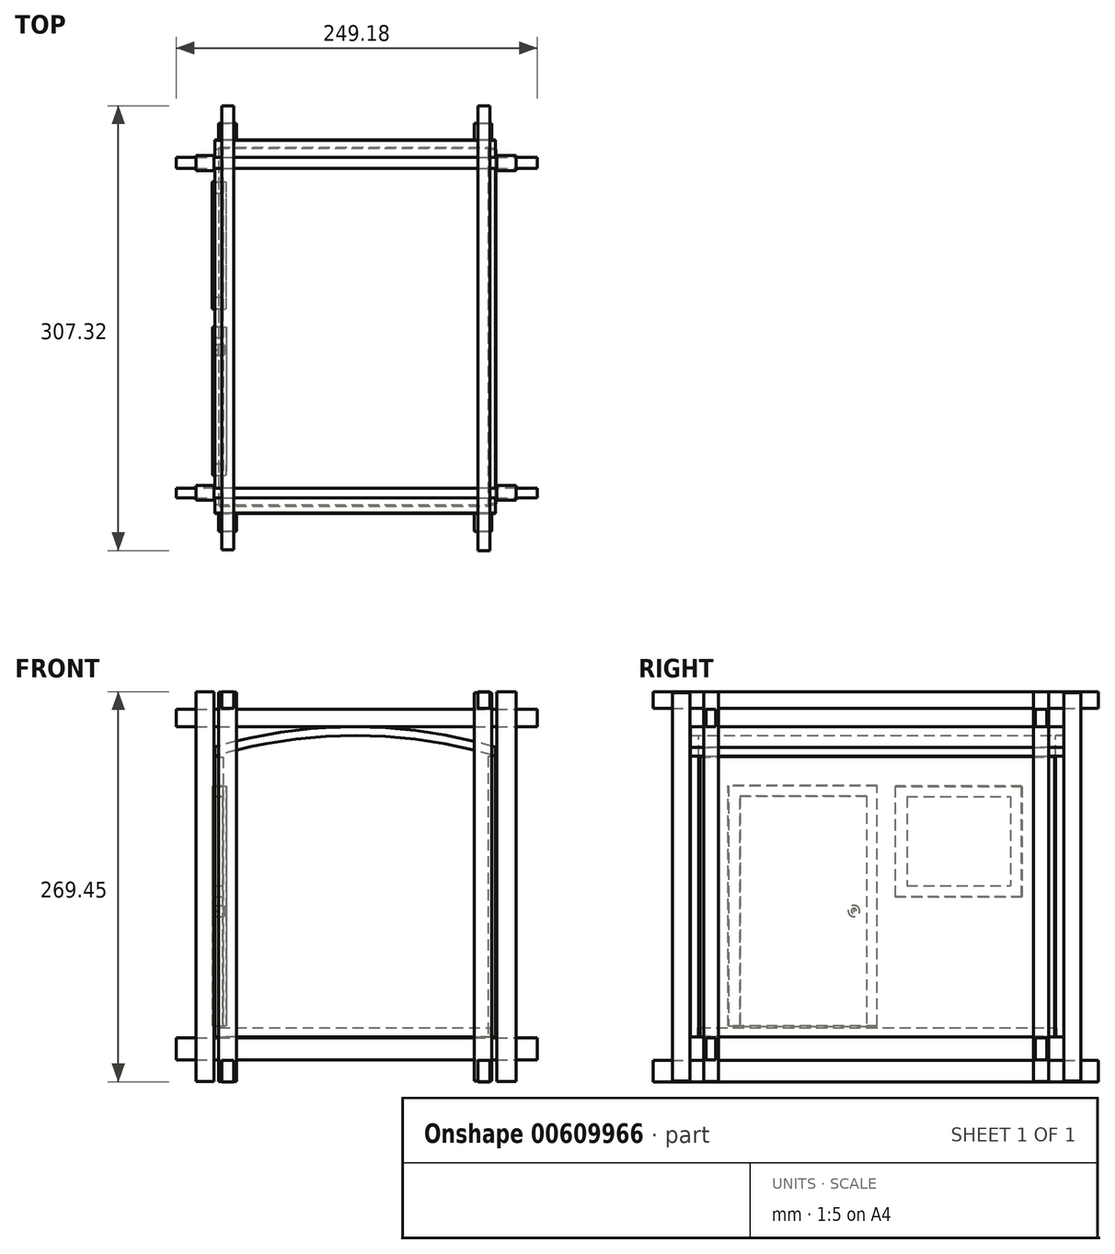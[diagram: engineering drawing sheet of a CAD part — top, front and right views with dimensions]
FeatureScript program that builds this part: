
annotation { "Feature Type Name" : "Feature", "Feature Type Description" : "" }
export const myFeature = defineFeature(function(context is Context, id is Id, definition is map)
    precondition{}
    {
        {
            var Q0;
            Q0=qCreatedBy(makeId("Front.planeOp"),FACE);
            var sketch = newSketch(context, id + "F0", { "sketchPlane" : qUnion([Q0])});
            skLineSegment(sketch, "E0", {"start": v(97.04, 97.04) * mm, "end": v(97.04, -96.89) * mm});
            skLineSegment(sketch, "E1", {"start": v(97.04, -96.89) * mm, "end": v(-96.89, -96.89) * mm});
            skLineSegment(sketch, "E2", {"start": v(-96.89, 97.04) * mm, "end": v(-96.89, -96.89) * mm});
            skArc(sketch, "E3", {"start": v(97.04, 97.04) * mm, "mid": v(0.08, 111.29) * mm, "end": v(-96.89, 97.04) * mm});
            skLineSegment(sketch, "E4", {"start": v(-96.89, 103.37) * mm, "end": v(-96.89, 97.04) * mm});
            skPoint(sketch, "E5.startSnap0", {"position": v(0.08, 111.29) * mm});
            skArc(sketch, "E6", {"start": v(97.04, 103.19) * mm, "mid": v(0.09, 117.3) * mm, "end": v(-96.89, 103.37) * mm});
            skLineSegment(sketch, "E7", {"start": v(97.04, 103.19) * mm, "end": v(97.04, 97.04) * mm});
            skSolve(sketch);
        }
        {
            var Q0;
            Q0=qCreatedBy(makeId("Right.planeOp"),FACE);
            var sketch = newSketch(context, id + "F1", { "sketchPlane" : qUnion([Q0])});
            skLineSegment(sketch, "E8.bottom", {"start": v(-124, 96.59) * mm, "end": v(124, 96.59) * mm});
            skLineSegment(sketch, "E8.top", {"start": v(-124, -96.59) * mm, "end": v(124, -96.59) * mm});
            skLineSegment(sketch, "E8.left", {"start": v(-124, 96.59) * mm, "end": v(-124, -96.59) * mm});
            skLineSegment(sketch, "E8.right", {"start": v(124, 96.59) * mm, "end": v(124, -96.59) * mm});
            skPoint(sketch, "E8.middle", {"position": v(0, 0) * mm});
            skLineSegment(sketch, "E9.bottom", {"start": v(100.14, 0) * mm, "end": v(11.51, 0) * mm});
            skLineSegment(sketch, "E9.top", {"start": v(100.14, 76.42) * mm, "end": v(11.51, 76.42) * mm});
            skLineSegment(sketch, "E9.left", {"start": v(100.14, 0) * mm, "end": v(100.14, 76.42) * mm});
            skLineSegment(sketch, "E9.right", {"start": v(11.51, 0) * mm, "end": v(11.51, 76.42) * mm});
            skLineSegment(sketch, "E10.bottom", {"start": v(17.87, 69.87) * mm, "end": v(93.79, 69.87) * mm});
            skLineSegment(sketch, "E10.top", {"start": v(17.87, 6.55) * mm, "end": v(93.79, 6.55) * mm});
            skLineSegment(sketch, "E10.left", {"start": v(17.87, 69.87) * mm, "end": v(17.87, 6.55) * mm});
            skLineSegment(sketch, "E10.right", {"start": v(93.79, 69.87) * mm, "end": v(93.79, 6.55) * mm});
            skPoint(sketch, "E10.middle", {"position": v(55.83, 38.21) * mm});
            skSolve(sketch);
        }
        {
            var Q0;
            Q0=makeQuery(id+"F0.imprint","IMPRINT",FACE,{"disambiguationData":[TD([[makeQuery(id+"F0.imprint","IMPRINT",EDGE,{"derivedFrom":sQuery(id+"F0.wireOp",EDGE,"E0")}),-1.0]])]});
            var sketch = newSketch(context, id + "F2", { "sketchPlane" : qUnion([Q0])});
            skSolve(sketch);
        }
        {
            var Q0;
            Q0=makeQuery(id+"F0.imprint","IMPRINT",FACE,{"disambiguationData":[TD([[makeQuery(id+"F0.imprint","IMPRINT",EDGE,{"derivedFrom":sQuery(id+"F0.wireOp",EDGE,"E0")}),-1.0]])]});
            extrude(context, id + "F3", {"entities" : qUnion([Q0]), "oppositeDirection" : true, "depth" : 128.86 * mm, "offsetDistance" : 25.4 * mm, "hasSecondDirection" : true, "secondDirectionOppositeDirection" : true, "secondDirectionDepth" : 123.07 * mm});
        }
        {
            var Q0;
            Q0=qCreatedBy(makeId("Top.planeOp"),FACE);
            var sketch = newSketch(context, id + "F4", { "sketchPlane" : qUnion([Q0])});
            skLineSegment(sketch, "E11.bottom", {"start": v(-93.76, -123.94) * mm, "end": v(93.76, -123.94) * mm});
            skLineSegment(sketch, "E11.top", {"start": v(-93.76, 123.94) * mm, "end": v(93.76, 123.94) * mm});
            skLineSegment(sketch, "E11.left", {"start": v(-93.76, -123.94) * mm, "end": v(-93.76, 123.94) * mm});
            skLineSegment(sketch, "E11.right", {"start": v(93.76, -123.94) * mm, "end": v(93.76, 123.94) * mm});
            skPoint(sketch, "E11.middle", {"position": v(0, 0) * mm});
            skSolve(sketch);
        }
        {
            var Q0;
            Q0=makeQuery(id+"F4.imprint","IMPRINT",FACE,{"disambiguationData":[TD([[makeQuery(id+"F4.imprint","IMPRINT",EDGE,{"derivedFrom":sQuery(id+"F4.wireOp",EDGE,"E11.bottom")}),1.0]])]});
            extrude(context, id + "F5", {"entities" : qUnion([Q0]), "oppositeDirection" : true, "depth" : 97.05 * mm, "offsetDistance" : 25.4 * mm, "hasSecondDirection" : true, "secondDirectionOppositeDirection" : true, "secondDirectionDepth" : 90.61 * mm});
        }
        {
            var Q0;
            Q0=makeQuery(id+"F0.imprint","IMPRINT",FACE,{"disambiguationData":[TD([[makeQuery(id+"F0.imprint","IMPRINT",EDGE,{"derivedFrom":sQuery(id+"F0.wireOp",EDGE,"E3")}),-1.0]])]});
            extrude(context, id + "F6", {"entities" : qUnion([Q0]), "depth" : 128.9 * mm, "offsetDistance" : 25.4 * mm, "hasSecondDirection" : true, "secondDirectionOppositeDirection" : true, "secondDirectionDepth" : 128.7 * mm});
        }
        {
            var Q0;
            Q0=makeQuery(id+"F2.imprint","IMPRINT",FACE,{"disambiguationData":[TD([[makeQuery(id+"F2.imprint","IMPRINT",EDGE,{"derivedFrom":makeQuery(id+"F0.imprint","IMPRINT",EDGE,{"derivedFrom":sQuery(id+"F0.wireOp",EDGE,"E0")})}),-1.0]])]});
            extrude(context, id + "F7", {"entities" : qUnion([Q0]), "depth" : 129.08 * mm, "offsetDistance" : 25.4 * mm, "hasSecondDirection" : true, "secondDirectionOppositeDirection" : false, "secondDirectionDepth" : 123.47 * mm});
        }
        {
            var Q0;
            Q0=qCreatedBy(makeId("Right.planeOp"),FACE);
            var sketch = newSketch(context, id + "F8", { "sketchPlane" : qUnion([Q0])});
            skLineSegment(sketch, "E12.bottom", {"start": v(122.43, 96.89) * mm, "end": v(-122.43, 96.89) * mm});
            skLineSegment(sketch, "E12.top", {"start": v(122.43, -96.89) * mm, "end": v(-122.43, -96.89) * mm});
            skLineSegment(sketch, "E12.left", {"start": v(122.43, 96.89) * mm, "end": v(122.43, -96.89) * mm});
            skLineSegment(sketch, "E12.right", {"start": v(-122.43, 96.89) * mm, "end": v(-122.43, -96.89) * mm});
            skPoint(sketch, "E12.middle", {"position": v(0, 0) * mm});
            skSolve(sketch);
        }
        {
            var Q0;
            Q0=qSketchRegion(id+"F8",true);
            extrude(context, id + "F9", {"entities" : qUnion([Q0]), "depth" : 97.34 * mm, "offsetDistance" : 25.4 * mm, "hasSecondDirection" : true, "secondDirectionOppositeDirection" : false, "secondDirectionDepth" : 91.88 * mm});
        }
        {
            var Q0;
            Q0=qCreatedBy(makeId("Right.planeOp"),FACE);
            var sketch = newSketch(context, id + "F10", { "sketchPlane" : qUnion([Q0])});
            skLineSegment(sketch, "E13.bottom", {"start": v(-122.74, 96.39) * mm, "end": v(122.74, 96.39) * mm});
            skLineSegment(sketch, "E13.top", {"start": v(-122.74, -96.39) * mm, "end": v(122.74, -96.39) * mm});
            skLineSegment(sketch, "E13.left", {"start": v(-122.74, 96.39) * mm, "end": v(-122.74, -96.39) * mm});
            skLineSegment(sketch, "E13.right", {"start": v(122.74, 96.39) * mm, "end": v(122.74, -96.39) * mm});
            skPoint(sketch, "E13.middle", {"position": v(0, 0) * mm});
            skLineSegment(sketch, "E14.bottom", {"start": v(99.68, 0) * mm, "end": v(12.53, 0) * mm});
            skLineSegment(sketch, "E14.top", {"start": v(99.68, 76.43) * mm, "end": v(12.53, 76.43) * mm});
            skLineSegment(sketch, "E14.left", {"start": v(99.68, 0) * mm, "end": v(99.68, 76.43) * mm});
            skLineSegment(sketch, "E14.right", {"start": v(12.53, 0) * mm, "end": v(12.53, 76.43) * mm});
            skLineSegment(sketch, "E15.bottom", {"start": v(20.07, 69.11) * mm, "end": v(92.14, 69.11) * mm});
            skLineSegment(sketch, "E15.top", {"start": v(20.07, 7.32) * mm, "end": v(92.14, 7.32) * mm});
            skLineSegment(sketch, "E15.left", {"start": v(20.07, 69.11) * mm, "end": v(20.07, 7.32) * mm});
            skLineSegment(sketch, "E15.right", {"start": v(92.14, 69.11) * mm, "end": v(92.14, 7.32) * mm});
            skPoint(sketch, "E15.middle", {"position": v(56.1, 38.22) * mm});
            skLineSegment(sketch, "E16", {"start": v(0, 0) * mm, "end": v(0, -89.44) * mm});
            skLineSegment(sketch, "E17.bottom", {"start": v(0, -89.44) * mm, "end": v(-102.94, -89.44) * mm});
            skLineSegment(sketch, "E17.top", {"start": v(0, 76.65) * mm, "end": v(-102.94, 76.65) * mm});
            skLineSegment(sketch, "E17.left", {"start": v(0, -89.44) * mm, "end": v(0, 76.65) * mm});
            skLineSegment(sketch, "E17.right", {"start": v(-102.94, -89.44) * mm, "end": v(-102.94, 76.65) * mm});
            skSolve(sketch);
        }
        {
            var Q0;
            Q0=makeQuery(id+"F10.imprint","IMPRINT",FACE,{"disambiguationData":[TD([[makeQuery(id+"F10.imprint","IMPRINT",EDGE,{"derivedFrom":sQuery(id+"F10.wireOp",EDGE,"E13.bottom")}),-1.0]])]});
            extrude(context, id + "F11", {"entities" : qUnion([Q0]), "operationType" : NewBodyOperationType.ADD, "oppositeDirection" : true, "depth" : 96.6 * mm, "offsetDistance" : 25.4 * mm, "hasSecondDirection" : true, "secondDirectionOppositeDirection" : true, "secondDirectionDepth" : 90.9 * mm});
        }
        {
            var Q0;
            Q0=makeQuery(id+"F10.imprint","IMPRINT",FACE,{"disambiguationData":[TD([[makeQuery(id+"F10.imprint","IMPRINT",EDGE,{"derivedFrom":sQuery(id+"F10.wireOp",EDGE,"E14.bottom")}),-1.0]])]});
            var Q1;
            Q1=qSketchRegion(id+"F10",true);
            extrude(context, id + "F12", {"entities" : qUnion([Q0, Q1]), "depth" : 25.4 * mm, "offsetDistance" : 25.4 * mm});
        }
        {
            var Q0;
            Q0=makeQuery(id+"F12.opExtrude","SWEPT_BODY",BODY,{"disambiguationData":[OSD([sQuery(id+"F10.wireOp",EDGE,"E13.bottom"),sQuery(id+"F10.wireOp",EDGE,"E13.top"),sQuery(id+"F10.wireOp",EDGE,"E13.left"),sQuery(id+"F10.wireOp",EDGE,"E13.right"),sQuery(id+"F10.wireOp",EDGE,"E15.bottom"),sQuery(id+"F10.wireOp",EDGE,"E15.top"),sQuery(id+"F10.wireOp",EDGE,"E15.left"),sQuery(id+"F10.wireOp",EDGE,"E15.right"),sQuery(id+"F10.wireOp",EDGE,"E17.bottom"),sQuery(id+"F10.wireOp",EDGE,"E17.top"),sQuery(id+"F10.wireOp",EDGE,"E17.left"),sQuery(id+"F10.wireOp",EDGE,"E17.right")])]});
            deleteBodies(context, id + "F13", {"entities" : qUnion([Q0])});
        }
        {
            var Q0;
            Q0=qCreatedBy(makeId("Right.planeOp"),FACE);
            var sketch = newSketch(context, id + "F14", { "sketchPlane" : qUnion([Q0])});
            skLineSegment(sketch, "E18.bottom", {"start": v(12.24, 76.08) * mm, "end": v(100.02, 76.08) * mm});
            skLineSegment(sketch, "E18.top", {"start": v(12.24, -0.18) * mm, "end": v(100.02, -0.18) * mm});
            skLineSegment(sketch, "E18.left", {"start": v(12.24, 76.08) * mm, "end": v(12.24, -0.18) * mm});
            skLineSegment(sketch, "E18.right", {"start": v(100.02, 76.08) * mm, "end": v(100.02, -0.18) * mm});
            skLineSegment(sketch, "E19.bottom", {"start": v(20.4, 68.99) * mm, "end": v(92.04, 68.99) * mm});
            skLineSegment(sketch, "E19.top", {"start": v(20.4, 7.45) * mm, "end": v(92.04, 7.45) * mm});
            skLineSegment(sketch, "E19.left", {"start": v(20.4, 68.99) * mm, "end": v(20.4, 7.45) * mm});
            skLineSegment(sketch, "E19.right", {"start": v(92.04, 68.99) * mm, "end": v(92.04, 7.45) * mm});
            skSolve(sketch);
        }
        {
            var Q0;
            Q0=makeQuery(id+"F14.imprint","IMPRINT",FACE,{"disambiguationData":[TD([[makeQuery(id+"F14.imprint","IMPRINT",EDGE,{"derivedFrom":sQuery(id+"F14.wireOp",EDGE,"E18.bottom")}),-1.0]])]});
            extrude(context, id + "F15", {"entities" : qUnion([Q0]), "oppositeDirection" : true, "depth" : 98.51 * mm, "offsetDistance" : 25.4 * mm, "hasSecondDirection" : true, "secondDirectionOppositeDirection" : true, "secondDirectionDepth" : 88.94 * mm});
        }
        {
            var Q0;
            Q0=qCreatedBy(makeId("Right.planeOp"),FACE);
            var sketch = newSketch(context, id + "F16", { "sketchPlane" : qUnion([Q0])});
            skLineSegment(sketch, "E20.bottom", {"start": v(-94.62, 69.34) * mm, "end": v(-7.44, 69.34) * mm});
            skLineSegment(sketch, "E20.top", {"start": v(-94.62, -89.54) * mm, "end": v(-7.44, -89.54) * mm});
            skLineSegment(sketch, "E20.left", {"start": v(-94.62, 69.34) * mm, "end": v(-94.62, -89.54) * mm});
            skLineSegment(sketch, "E20.right", {"start": v(-7.44, 69.34) * mm, "end": v(-7.44, -89.54) * mm});
            skPoint(sketch, "E20.middle", {"position": v(-51.03, -10.1) * mm});
            skSolve(sketch);
        }
        {
            var Q0;
            Q0=makeQuery(id+"F16.imprint","IMPRINT",FACE,{"disambiguationData":[TD([[makeQuery(id+"F16.imprint","IMPRINT",EDGE,{"derivedFrom":sQuery(id+"F16.wireOp",EDGE,"E20.bottom")}),-1.0]])]});
            extrude(context, id + "F17", {"entities" : qUnion([Q0]), "oppositeDirection" : true, "depth" : 96.36 * mm, "offsetDistance" : 25.4 * mm, "hasSecondDirection" : true, "secondDirectionOppositeDirection" : true, "secondDirectionDepth" : 91.7 * mm});
        }
        {
            var Q0;
            Q0=qCreatedBy(makeId("Right.planeOp"),FACE);
            var sketch = newSketch(context, id + "F18", { "sketchPlane" : qUnion([Q0])});
            skLineSegment(sketch, "E21", {"start": v(-0.3, -89.2) * mm, "end": v(-0.3, 76.5) * mm});
            skLineSegment(sketch, "E22", {"start": v(-0.3, 76.5) * mm, "end": v(-102.83, 76.5) * mm});
            skLineSegment(sketch, "E23", {"start": v(-102.83, 76.5) * mm, "end": v(-102.83, -89.33) * mm});
            skLineSegment(sketch, "E24", {"start": v(-102.83, -89.33) * mm, "end": v(-94.8, -89.33) * mm});
            skLineSegment(sketch, "E25", {"start": v(-94.8, -89.33) * mm, "end": v(-94.8, 69.34) * mm});
            skLineSegment(sketch, "E26", {"start": v(-7.57, 69.34) * mm, "end": v(-94.8, 69.34) * mm});
            skLineSegment(sketch, "E27", {"start": v(-7.57, 69.34) * mm, "end": v(-7.57, -89.2) * mm});
            skLineSegment(sketch, "E28", {"start": v(-7.57, -89.2) * mm, "end": v(-0.3, -89.2) * mm});
            skSolve(sketch);
        }
        {
            var Q0;
            Q0=makeQuery(id+"F18.imprint","IMPRINT",FACE,{"disambiguationData":[TD([[makeQuery(id+"F18.imprint","IMPRINT",EDGE,{"derivedFrom":sQuery(id+"F18.wireOp",EDGE,"E21")}),1.0]])]});
            extrude(context, id + "F19", {"entities" : qUnion([Q0]), "oppositeDirection" : true, "depth" : 98.47 * mm, "offsetDistance" : 25.4 * mm, "hasSecondDirection" : true, "secondDirectionOppositeDirection" : true, "secondDirectionDepth" : 88.82 * mm});
        }
        {
            var Q0;
            Q0=qCreatedBy(makeId("Right.planeOp"),FACE);
            var sketch = newSketch(context, id + "F20", { "sketchPlane" : qUnion([Q0])});
            skCircle(sketch, "E29", {"center": v(-16.12, -10) * mm, "radius": 3.9 * mm});
            skSolve(sketch);
        }
        {
            var Q0;
            Q0=makeQuery(id+"F20.imprint","IMPRINT",FACE,{"disambiguationData":[TD([[makeQuery(id+"F20.imprint","IMPRINT",EDGE,{"derivedFrom":sQuery(id+"F20.wireOp",EDGE,"E29")}),1.0]])]});
            var Q1;
            Q1=qSketchRegion(id+"F2",true);
            extrude(context, id + "F21", {"entities" : qUnion([Q0, Q1]), "oppositeDirection" : true, "depth" : 98.42 * mm, "offsetDistance" : 25.4 * mm, "hasSecondDirection" : true, "secondDirectionOppositeDirection" : true, "secondDirectionDepth" : 89.62 * mm});
        }
        {
            var Q0;
            Q0=makeQuery(id+"F21.opExtrude","SWEPT_FACE",FACE,{"disambiguationData":[OSD([sQuery(id+"F20.wireOp",EDGE,"E29")])]});
            fillet(context, id + "F22", {"entities" : qUnion([Q0]), "radius" : 2.1 * mm, "tangentPropagation" : true, "allowEdgeOverflow" : false});
        }
        {
            var Q0;
            Q0=qCreatedBy(makeId("Right.planeOp"),FACE);
            var sketch = newSketch(context, id + "F23", { "sketchPlane" : qUnion([Q0])});
            skLineSegment(sketch, "E30", {"start": v(-120, 141.52) * mm, "end": v(-120, -127.79) * mm});
            skLineSegment(sketch, "E31", {"start": v(107.83, -127.79) * mm, "end": v(107.83, 141.52) * mm});
            skLineSegment(sketch, "E32", {"start": v(118.18, 141.52) * mm, "end": v(107.83, 141.52) * mm});
            skLineSegment(sketch, "E33", {"start": v(118.18, -127.79) * mm, "end": v(118.18, 141.52) * mm});
            skLineSegment(sketch, "E34", {"start": v(107.83, -127.79) * mm, "end": v(118.18, -127.79) * mm});
            skLineSegment(sketch, "E35", {"start": v(-109.65, 141.52) * mm, "end": v(-120, 141.52) * mm});
            skLineSegment(sketch, "E36", {"start": v(-109.65, -127.79) * mm, "end": v(-109.65, 141.52) * mm});
            skLineSegment(sketch, "E37", {"start": v(-120, -127.79) * mm, "end": v(-109.65, -127.79) * mm});
            skSolve(sketch);
        }
        {
            var Q0;
            Q0=makeQuery(id+"F23.imprint","IMPRINT",FACE,{"disambiguationData":[TD([[makeQuery(id+"F23.imprint","IMPRINT",EDGE,{"derivedFrom":sQuery(id+"F23.wireOp",EDGE,"E31")}),-1.0]])]});
            var Q1;
            Q1=makeQuery(id+"F23.imprint","IMPRINT",FACE,{"disambiguationData":[TD([[makeQuery(id+"F23.imprint","IMPRINT",EDGE,{"derivedFrom":sQuery(id+"F23.wireOp",EDGE,"E30")}),1.0]])]});
            extrude(context, id + "F24", {"entities" : qUnion([Q0, Q1]), "depth" : 111.1 * mm, "offsetDistance" : 25.4 * mm, "hasSecondDirection" : true, "secondDirectionOppositeDirection" : false, "secondDirectionDepth" : 97.8 * mm});
        }
        {
            var Q0;
            Q0=qSketchRegion(id+"F23",true);
            extrude(context, id + "F25", {"entities" : qUnion([Q0]), "oppositeDirection" : true, "depth" : 109.74 * mm, "offsetDistance" : 25.4 * mm, "hasSecondDirection" : true, "secondDirectionOppositeDirection" : true, "secondDirectionDepth" : 97.35 * mm});
        }
        {
            var Q0;
            Q0=qCreatedBy(makeId("Front.planeOp"),FACE);
            var sketch = newSketch(context, id + "F26", { "sketchPlane" : qUnion([Q0])});
            skLineSegment(sketch, "E38", {"start": v(-94.12, -127.59) * mm, "end": v(-81.8, -127.59) * mm});
            skLineSegment(sketch, "E39", {"start": v(-94.12, 141.07) * mm, "end": v(-94.12, -127.59) * mm});
            skLineSegment(sketch, "E40", {"start": v(-81.8, 141.07) * mm, "end": v(-81.8, -127.59) * mm});
            skLineSegment(sketch, "E41", {"start": v(-81.8, 141.07) * mm, "end": v(-94.12, 141.07) * mm});
            skLineSegment(sketch, "E42", {"start": v(94.32, -127.39) * mm, "end": v(82.4, -127.39) * mm});
            skLineSegment(sketch, "E43", {"start": v(94.32, 140.88) * mm, "end": v(94.32, -127.39) * mm});
            skLineSegment(sketch, "E44", {"start": v(82.4, 140.88) * mm, "end": v(82.4, -127.39) * mm});
            skLineSegment(sketch, "E45", {"start": v(82.4, 140.88) * mm, "end": v(94.32, 140.88) * mm});
            skSolve(sketch);
        }
        {
            var Q0;
            Q0=makeQuery(id+"F26.imprint","IMPRINT",FACE,{"disambiguationData":[TD([[makeQuery(id+"F26.imprint","IMPRINT",EDGE,{"derivedFrom":sQuery(id+"F26.wireOp",EDGE,"E42")}),-1.0]])]});
            var Q1;
            Q1=makeQuery(id+"F26.imprint","IMPRINT",FACE,{"disambiguationData":[TD([[makeQuery(id+"F26.imprint","IMPRINT",EDGE,{"derivedFrom":sQuery(id+"F26.wireOp",EDGE,"E38")}),1.0]])]});
            extrude(context, id + "F27", {"entities" : qUnion([Q0, Q1]), "oppositeDirection" : true, "depth" : 140.48 * mm, "offsetDistance" : 25.4 * mm, "hasSecondDirection" : true, "secondDirectionOppositeDirection" : true, "secondDirectionDepth" : 128.89 * mm});
        }
        {
            var Q0;
            Q0=qSketchRegion(id+"F26",true);
            extrude(context, id + "F28", {"entities" : qUnion([Q0]), "depth" : 141.5 * mm, "offsetDistance" : 25.4 * mm, "hasSecondDirection" : true, "secondDirectionOppositeDirection" : false, "secondDirectionDepth" : 129.24 * mm});
        }
        {
            var Q0;
            Q0=qCreatedBy(makeId("Top.planeOp"),FACE);
            var sketch = newSketch(context, id + "F29", { "sketchPlane" : qUnion([Q0])});
            skLineSegment(sketch, "E46", {"start": v(84.7, -154.81) * mm, "end": v(93.11, -154.81) * mm});
            skLineSegment(sketch, "E47", {"start": v(93.11, -154.81) * mm, "end": v(93.11, 152.5) * mm});
            skLineSegment(sketch, "E48", {"start": v(84.7, 152.5) * mm, "end": v(84.7, -154.81) * mm});
            skLineSegment(sketch, "E49", {"start": v(84.7, 152.5) * mm, "end": v(93.11, 152.5) * mm});
            skLineSegment(sketch, "E50", {"start": v(-92, -154.3) * mm, "end": v(-83.6, -154.3) * mm});
            skLineSegment(sketch, "E51", {"start": v(-92, -154.3) * mm, "end": v(-92, 152.5) * mm});
            skLineSegment(sketch, "E52", {"start": v(-83.6, 152.5) * mm, "end": v(-83.6, -154.3) * mm});
            skLineSegment(sketch, "E53", {"start": v(-92, 152.5) * mm, "end": v(-83.6, 152.5) * mm});
            skSolve(sketch);
        }
        {
            var Q0;
            Q0=makeQuery(id+"F29.imprint","IMPRINT",FACE,{"disambiguationData":[TD([[makeQuery(id+"F29.imprint","IMPRINT",EDGE,{"derivedFrom":sQuery(id+"F29.wireOp",EDGE,"E50")}),1.0]])]});
            var Q1;
            Q1=makeQuery(id+"F29.imprint","IMPRINT",FACE,{"disambiguationData":[TD([[makeQuery(id+"F29.imprint","IMPRINT",EDGE,{"derivedFrom":sQuery(id+"F29.wireOp",EDGE,"E46")}),1.0]])]});
            extrude(context, id + "F30", {"entities" : qUnion([Q0, Q1]), "depth" : 141.52 * mm, "offsetDistance" : 25.4 * mm, "hasSecondDirection" : true, "secondDirectionOppositeDirection" : false, "secondDirectionDepth" : 129.96 * mm});
        }
        {
            var Q0;
            Q0=qSketchRegion(id+"F29",true);
            extrude(context, id + "F31", {"entities" : qUnion([Q0]), "oppositeDirection" : true, "depth" : 127.93 * mm, "offsetDistance" : 25.4 * mm, "hasSecondDirection" : true, "secondDirectionOppositeDirection" : true, "secondDirectionDepth" : 113.15 * mm});
        }
        {
            var Q0;
            Q0=qCreatedBy(makeId("Top.planeOp"),FACE);
            var sketch = newSketch(context, id + "F32", { "sketchPlane" : qUnion([Q0])});
            skLineSegment(sketch, "E54", {"start": v(-123.38, 109.18) * mm, "end": v(-123.38, 116.87) * mm});
            skLineSegment(sketch, "E55", {"start": v(-123.38, 116.87) * mm, "end": v(125.8, 116.87) * mm});
            skLineSegment(sketch, "E56", {"start": v(125.8, 116.87) * mm, "end": v(125.8, 109.18) * mm});
            skLineSegment(sketch, "E57", {"start": v(-123.38, 109.18) * mm, "end": v(125.8, 109.18) * mm});
            skLineSegment(sketch, "E58", {"start": v(125.8, -111.59) * mm, "end": v(-123.38, -111.59) * mm});
            skLineSegment(sketch, "E59", {"start": v(-123.38, -118.28) * mm, "end": v(125.8, -118.28) * mm});
            skLineSegment(sketch, "E60", {"start": v(125.8, -118.28) * mm, "end": v(125.8, -111.59) * mm});
            skLineSegment(sketch, "E61", {"start": v(-123.38, -111.59) * mm, "end": v(-123.38, -118.28) * mm});
            skSolve(sketch);
        }
        {
            var Q0;
            Q0=makeQuery(id+"F32.imprint","IMPRINT",FACE,{"disambiguationData":[TD([[makeQuery(id+"F32.imprint","IMPRINT",EDGE,{"derivedFrom":sQuery(id+"F32.wireOp",EDGE,"E54")}),-1.0]])]});
            var Q1;
            Q1=makeQuery(id+"F32.imprint","IMPRINT",FACE,{"disambiguationData":[TD([[makeQuery(id+"F32.imprint","IMPRINT",EDGE,{"derivedFrom":sQuery(id+"F32.wireOp",EDGE,"E58")}),1.0]])]});
            extrude(context, id + "F33", {"entities" : qUnion([Q0, Q1]), "oppositeDirection" : true, "depth" : 112.96 * mm, "offsetDistance" : 25.4 * mm, "hasSecondDirection" : true, "secondDirectionOppositeDirection" : true, "secondDirectionDepth" : 97.54 * mm});
        }
        {
            var Q0;
            Q0=qSketchRegion(id+"F32",true);
            extrude(context, id + "F34", {"entities" : qUnion([Q0]), "depth" : 129.6 * mm, "offsetDistance" : 25.4 * mm, "hasSecondDirection" : true, "secondDirectionOppositeDirection" : false, "secondDirectionDepth" : 117.4 * mm});
        }
    });
